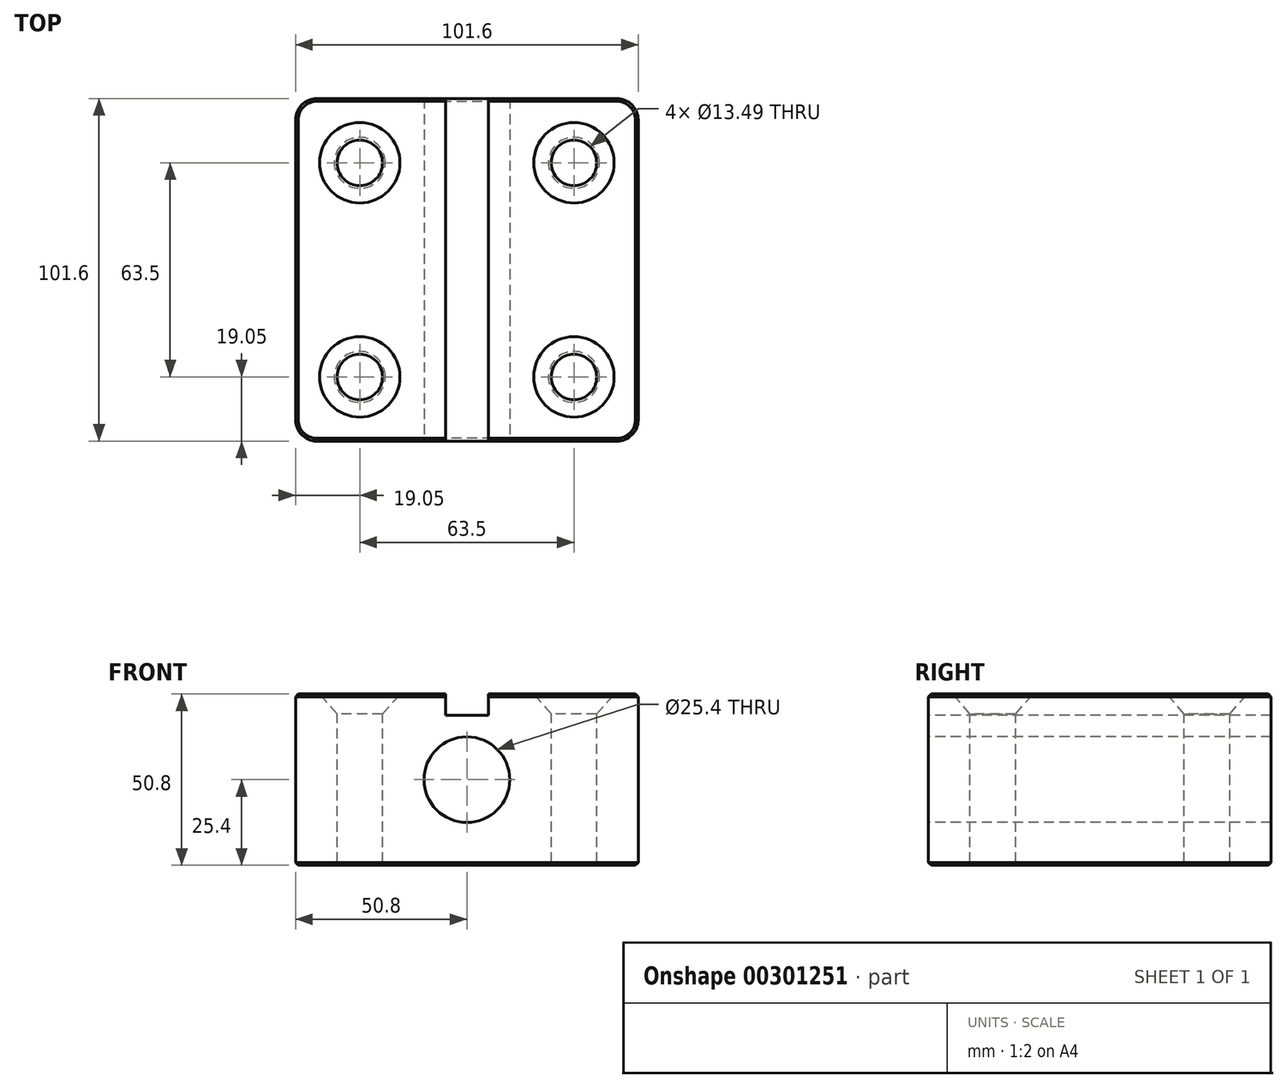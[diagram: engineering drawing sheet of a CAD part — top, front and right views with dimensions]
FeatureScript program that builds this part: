
annotation { "Feature Type Name" : "Feature", "Feature Type Description" : "" }
export const myFeature = defineFeature(function(context is Context, id is Id, definition is map)
    precondition{}
    {
        {
            var Q0;
            Q0=qCreatedBy(makeId("Front.planeOp"),FACE);
            var sketch = newSketch(context, id + "F0", { "sketchPlane" : qUnion([Q0])});
            skLineSegment(sketch, "E0.bottom", {"start": v(-50.8, 25.4) * mm, "end": v(50.8, 25.4) * mm});
            skLineSegment(sketch, "E0.top", {"start": v(-50.8, -25.4) * mm, "end": v(50.8, -25.4) * mm});
            skLineSegment(sketch, "E0.left", {"start": v(-50.8, 25.4) * mm, "end": v(-50.8, -25.4) * mm});
            skLineSegment(sketch, "E0.right", {"start": v(50.8, 25.4) * mm, "end": v(50.8, -25.4) * mm});
            skLineSegment(sketch, "E1.bottom", {"start": v(50.8, 25.4) * mm, "end": v(50.8, 25.4) * mm});
            skLineSegment(sketch, "E1.top", {"start": v(50.8, -25.4) * mm, "end": v(50.8, -25.4) * mm});
            skLineSegment(sketch, "E2.top", {"start": v(12.6, 25.4) * mm, "end": v(50.8, 25.4) * mm});
            skSolve(sketch);
        }
        {
            var Q0;
            Q0=makeQuery(id+"F0.imprint","IMPRINT",FACE,{"disambiguationData":[TD([[makeQuery(id+"F0.imprint","IMPRINT",EDGE,{"derivedFrom":sQuery(id+"F0.wireOp",EDGE,"E0.bottom")}),-1.0]])]});
            extrude(context, id + "F1", {"entities" : qUnion([Q0]), "endBound" : BoundingType.SYMMETRIC, "depth" : 101.6 * mm});
        }
        {
            var Q0;
            Q0=makeQuery(id+"F1.opExtrude","SWEPT_FACE",FACE,{"disambiguationData":[OSD([sQuery(id+"F0.wireOp",EDGE,"E0.bottom"),sQuery(id+"F0.wireOp",EDGE,"E2.top")])]});
            var sketch = newSketch(context, id + "F2", { "sketchPlane" : qUnion([Q0])});
            skPoint(sketch, "E3", {"position": v(-31.75, 31.75) * mm});
            skPoint(sketch, "E4.MirrorP", {"position": v(31.75, 31.75) * mm});
            skPoint(sketch, "E5.MirrorP", {"position": v(-31.75, -31.75) * mm});
            skPoint(sketch, "E6.MirrorP", {"position": v(31.75, -31.75) * mm});
            skSolve(sketch);
        }
        {
            var Q0;
            Q0=sQuery(id+"F2.wireOp",VERTEX,"E3");
            var Q1;
            Q1=sQuery(id+"F2.wireOp",VERTEX,"E4.MirrorP");
            var Q2;
            Q2=sQuery(id+"F2.wireOp",VERTEX,"E5.MirrorP");
            var Q3;
            Q3=sQuery(id+"F2.wireOp",VERTEX,"E6.MirrorP");
            var Q4;
            Q4=makeQuery(id+"F1.opExtrude","SWEPT_BODY",BODY,{"disambiguationData":[OSD([sQuery(id+"F0.wireOp",EDGE,"E0.bottom"),sQuery(id+"F0.wireOp",EDGE,"E0.top"),sQuery(id+"F0.wireOp",EDGE,"E0.left"),sQuery(id+"F0.wireOp",EDGE,"E0.right"),sQuery(id+"F0.wireOp",EDGE,"E2.top")])]});
            hole(context, id + "F3", {"style" : HoleStyle.C_SINK, "endStyle" : HoleEndStyle.THROUGH, "standardTappedOrClearance" : lookupTablePath({ "standard" : "ANSI", "fit" : "Normal (ASME)", "size" : "1/2", "type" : "Clearance" }), "standardBlindInLast" : lookupTablePath({ "fit" : "Free", "standard" : "ANSI", "size" : "1/2", "type" : "Clearance" }), "holeDiameter" : 13.5 * mm, "cSinkDiameter" : 23.83 * mm, "cSinkAngle" : 82 * degree, "tappedDepth" : 12.7 * mm, "tapClearance" : 3, "locations" : qUnion([Q0, Q1, Q2, Q3]), "scope" : qUnion([Q4])});
        }
        {
            var Q0;
            Q0=makeQuery(id+"F1.opExtrude","CAP_EDGE",EDGE,{"disambiguationData":[OSD([sQuery(id+"F0.wireOp",EDGE,"E0.left")])],"isStart":true});
            var Q1;
            Q1=makeQuery(id+"F1.opExtrude","CAP_EDGE",EDGE,{"disambiguationData":[OSD([sQuery(id+"F0.wireOp",EDGE,"E0.left")])],"isStart":false});
            var Q2;
            Q2=makeQuery(id+"F1.opExtrude","CAP_EDGE",EDGE,{"disambiguationData":[OSD([sQuery(id+"F0.wireOp",EDGE,"E0.right")])],"isStart":false});
            var Q3;
            Q3=makeQuery(id+"F1.opExtrude","CAP_EDGE",EDGE,{"disambiguationData":[OSD([sQuery(id+"F0.wireOp",EDGE,"E0.right")])],"isStart":true});
            fillet(context, id + "F4", {"entities" : qUnion([Q0, Q1, Q2, Q3]), "radius" : 6.35 * mm, "tangentPropagation" : true, "allowEdgeOverflow" : false});
        }
        {
            var Q0;
            Q0=makeQuery(id+"F1.opExtrude","SWEPT_FACE",FACE,{"disambiguationData":[OSD([sQuery(id+"F0.wireOp",EDGE,"E0.bottom"),sQuery(id+"F0.wireOp",EDGE,"E2.top")])]});
            var sketch = newSketch(context, id + "F5", { "sketchPlane" : qUnion([Q0])});
            skLineSegment(sketch, "E7", {"start": v(-6.35, 50.8) * mm, "end": v(-6.35, -50.8) * mm});
            skLineSegment(sketch, "E8", {"start": v(-6.35, -50.8) * mm, "end": v(6.35, -50.8) * mm});
            skLineSegment(sketch, "E9", {"start": v(6.35, -50.8) * mm, "end": v(6.35, 50.8) * mm});
            skLineSegment(sketch, "E10", {"start": v(6.35, 50.8) * mm, "end": v(-6.35, 50.8) * mm});
            skSolve(sketch);
        }
        {
            var Q0;
            Q0=makeQuery(id+"F5.imprint","IMPRINT",FACE,{"disambiguationData":[TD([[makeQuery(id+"F5.imprint","IMPRINT",EDGE,{"derivedFrom":sQuery(id+"F5.wireOp",EDGE,"E7")}),1.0]])]});
            extrude(context, id + "F6", {"entities" : qUnion([Q0]), "operationType" : NewBodyOperationType.REMOVE, "oppositeDirection" : true, "depth" : 6.35 * mm});
        }
        {
            var Q0;
            Q0=makeQuery(id+"F1.opExtrude","CAP_FACE",FACE,{"disambiguationData":[OSD([sQuery(id+"F0.wireOp",EDGE,"E0.bottom"),sQuery(id+"F0.wireOp",EDGE,"E0.top"),sQuery(id+"F0.wireOp",EDGE,"E0.left"),sQuery(id+"F0.wireOp",EDGE,"E0.right"),sQuery(id+"F0.wireOp",EDGE,"E2.top")])],"isStart":false});
            var sketch = newSketch(context, id + "F7", { "sketchPlane" : qUnion([Q0])});
            skCircle(sketch, "E11", {"center": v(0, 0) * mm, "radius": 12.7 * mm});
            skSolve(sketch);
        }
        {
            var Q0;
            Q0=makeQuery(id+"F7.imprint","IMPRINT",FACE,{"disambiguationData":[TD([[makeQuery(id+"F7.imprint","IMPRINT",EDGE,{"derivedFrom":sQuery(id+"F7.wireOp",EDGE,"E11")}),1.0]])]});
            extrude(context, id + "F8", {"entities" : qUnion([Q0]), "operationType" : NewBodyOperationType.REMOVE, "endBound" : BoundingType.THROUGH_ALL, "oppositeDirection" : true, "depth" : 25.4 * mm});
        }
        {
            var Q0;
            Q0=makeQuery(id+"F1.opExtrude","CAP_EDGE",EDGE,{"disambiguationData":[OSD([sQuery(id+"F0.wireOp",EDGE,"E0.bottom"),sQuery(id+"F0.wireOp",EDGE,"E2.top")])],"isStart":true});
            var Q1;
            Q1=makeQuery(id+"F1.opExtrude","SWEPT_EDGE",EDGE,{"disambiguationData":[OSD([sQuery(id+"F0.wireOp",EDGE,"E0.right"),sQuery(id+"F0.wireOp",EDGE,"E2.top")])]});
            var Q2;
            Q2=makeQuery(id+"F1.opExtrude","CAP_EDGE",EDGE,{"disambiguationData":[OSD([sQuery(id+"F0.wireOp",EDGE,"E0.bottom"),sQuery(id+"F0.wireOp",EDGE,"E2.top")])],"isStart":false});
            var Q3;
            Q3=makeQuery(id+"F1.opExtrude","SWEPT_EDGE",EDGE,{"disambiguationData":[OSD([sQuery(id+"F0.wireOp",EDGE,"E0.bottom"),sQuery(id+"F0.wireOp",EDGE,"E0.left")])]});
            var Q4;
            Q4=makeQuery(id+"F1.opExtrude","SWEPT_FACE",FACE,{"disambiguationData":[OSD([sQuery(id+"F0.wireOp",EDGE,"E0.top")])]});
            chamfer(context, id + "F9", {"entities" : qUnion([Q0, Q1, Q2, Q3, Q4]), "width" : 0.81 * mm, "tangentPropagation" : true});
        }
    });
